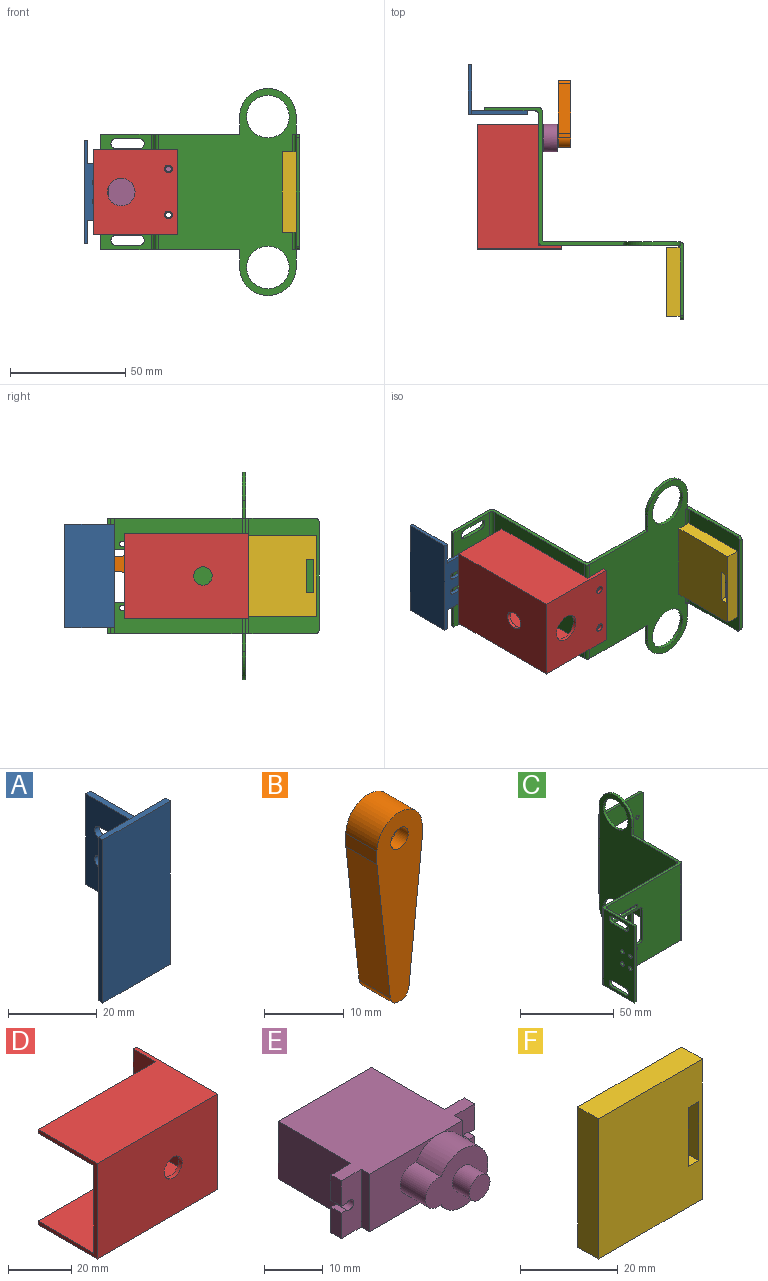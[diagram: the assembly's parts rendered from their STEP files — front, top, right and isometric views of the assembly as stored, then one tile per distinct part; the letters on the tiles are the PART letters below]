
ASSEMBLY  parts=6 mates=5
PART A: 18 faces, bbox 21.5x25.5x45 mm
  f0: plane 24x1.5mm, normal (0,0,1), area 36mm2, adj f3,f5,f6,f7
  f1: plane 24x1.5mm, normal (0,0,-1), area 36mm2, adj f3,f5,f6,f7
  f2: plane 45x21.5mm, normal (0,-1,0), area 967.5mm2, adj f4,f6,f16,f17
  f3: plane 45x21.5mm, normal (0,1,0), area 930mm2, adj f0,f1,f4,f6,f7,f16,f17
  f4: plane 45x1.5mm, normal (-1,0,0), area 67.5mm2, adj f2,f3,f16,f17
  f5: plane 25x1.5mm, normal (0,1,0), area 37.5mm2, adj f0,f1,f6,f7
  f6: plane 45x25.5mm, normal (1,0,0), area 549mm2, adj f0,f1,f2,f3,f5,f8,f9,f10
  f7: plane 25x24mm, normal (-1,0,0), area 481.5mm2, adj f0,f1,f3,f5,f8,f9,f10,f11
  f8: cylinder r=1.6mm len=3.2mm, axis (1,0,0), area 7.5mm2, adj f6,f7,f9,f11
  f9: plane 16x1.5mm, normal (0,0,-1), area 24mm2, adj f6,f7,f8,f10
  f10: cylinder r=1.6mm len=3.2mm, axis (1,0,0), area 7.5mm2, adj f6,f7,f9,f11
  f11: plane 16x1.5mm, normal (0,0,1), area 24mm2, adj f6,f7,f8,f10
  f12: cylinder r=1.6mm len=3.2mm, axis (1,0,0), area 7.5mm2, adj f6,f7,f13,f15
  f13: plane 16x1.5mm, normal (0,0,1), area 24mm2, adj f6,f7,f12,f14
  f14: cylinder r=1.6mm len=3.2mm, axis (1,0,0), area 7.5mm2, adj f6,f7,f13,f15
  f15: plane 16x1.5mm, normal (0,0,-1), area 24mm2, adj f6,f7,f12,f14
  f16: plane 21.5x1.5mm, normal (0,0,-1), area 32.3mm2, adj f2,f3,f4,f6
  f17: plane 21.5x1.5mm, normal (0,0,1), area 32.3mm2, adj f2,f3,f4,f6
PART B: 13 faces, bbox 8x5.5x29 mm
  f0: plane 5.5x0.31mm, normal (0,0,-1), area 1.7mm2, adj f3,f4,f11,f12
  f1: plane 5.5x2mm, normal (1,0,0), area 11mm2, adj f3,f4,f5,f10
  f2: plane 5.5x2mm, normal (-1,0,0), area 11mm2, adj f3,f4,f5,f9
  f3: plane 29x8mm, normal (0,1,0), area 148.8mm2, adj f0,f1,f2,f5,f6,f9,f10,f11
  f4: plane 29x8mm, normal (0,-1,0), area 159.3mm2, adj f0,f1,f2,f5,f8,f9,f10,f11
  f5: cylinder r=4mm len=8mm, axis (0,-1,0), area 69.1mm2, adj f1,f2,f3,f4
  f6: cylinder r=2.4mm len=4.8mm, axis (0,-1,0), area 52.8mm2, adj f3,f7
  f7: plane 4.8x4.8mm, normal (0,1,0), area 10.5mm2, adj f6,f8
  f8: cylinder r=1.55mm len=3.1mm, axis (0,1,0), area 19.5mm2, adj f4,f7
  f9: plane 21.66x5.5mm, normal (-0.99,0,-0.11), area 119.8mm2, adj f2,f3,f4,f11
  f10: plane 21.66x5.5mm, normal (0.99,0,-0.11), area 119.8mm2, adj f1,f3,f4,f12
  f11: cylinder r=1.5mm len=5.5mm, axis (0,1,0), area 12.1mm2, adj f0,f3,f4,f9
  f12: cylinder r=1.5mm len=5.5mm, axis (0,-1,0), area 12.1mm2, adj f0,f3,f4,f10
PART C: 72 faces, bbox 92x86.5x90 mm
  f0: plane 50x25mm, normal (1,0,0), area 1018.6mm2, adj f5,f6,f7,f37,f38,f39,f40,f41
  f1: plane 50x23.5mm, normal (-1,0,0), area 1033.6mm2, adj f5,f6,f7,f37,f38,f39,f40,f41
  f2: plane 50x30.5mm, normal (0,-1,0), area 1162.1mm2, adj f30,f31,f32,f33,f34,f35,f36,f51
  f3: plane 50x32mm, normal (0,1,0), area 1237.1mm2, adj f30,f31,f32,f33,f34,f35,f36,f51
  f4: plane 7.75x1.5mm, normal (0,1,0), area 11.6mm2, adj f21,f22,f28,f31
  f5: plane 60.5x60mm, normal (0,0,-1), area 178.5mm2, adj f0,f1,f7,f8,f20,f21,f22,f27
  f6: plane 60.5x60mm, normal (0,0,1), area 178.5mm2, adj f0,f1,f7,f8,f20,f21,f22,f26
  f7: plane 50x1.5mm, normal (0,-1,0), area 75mm2, adj f0,f1,f5,f6
  f8: plane 55.5x50mm, normal (0,1,0), area 2037.5mm2, adj f5,f6,f9,f10,f11,f12,f13,f14
  f9: cylinder r=1.2mm len=2.4mm, axis (0,1,0), area 5.7mm2, adj f8,f10,f19,f20
  f10: plane 18x1.5mm, normal (0,0,1), area 27mm2, adj f8,f9,f11,f20
  f11: cylinder r=1.2mm len=2.4mm, axis (0,1,0), area 5.7mm2, adj f8,f10,f19,f20
  f12: plane 25x1.5mm, normal (0,0,-1), area 37.5mm2, adj f8,f20,f68,f71
  f13: plane 20x1.5mm, normal (-1,0,0), area 30mm2, adj f8,f20,f68,f69
  f14: plane 25x1.5mm, normal (0,0,1), area 37.5mm2, adj f8,f20,f69,f70
  f15: plane 18x1.5mm, normal (0,0,-1), area 27mm2, adj f8,f16,f18,f20
  f16: cylinder r=1.2mm len=2.4mm, axis (0,1,0), area 5.7mm2, adj f8,f15,f17,f20
  f17: plane 18x1.5mm, normal (0,0,1), area 27mm2, adj f8,f16,f18,f20
  f18: cylinder r=1.2mm len=2.4mm, axis (0,1,0), area 5.7mm2, adj f8,f15,f17,f20
  f19: plane 18x1.5mm, normal (0,0,-1), area 27mm2, adj f8,f9,f11,f20
  f20: plane 55.5x50mm, normal (0,-1,0), area 2071mm2, adj f5,f6,f9,f10,f11,f12,f13,f14
  f21: plane 90x58.5mm, normal (-1,0,0), area 3228.8mm2, adj f4,f5,f6,f23,f24,f25,f26,f27
  f22: plane 90x60mm, normal (1,0,0), area 3228.8mm2, adj f4,f5,f6,f23,f24,f25,f26,f27
  f23: plane 7.75x1.5mm, normal (0,1,0), area 11.6mm2, adj f21,f22,f25,f30
  f24: cylinder r=9.25mm len=18.5mm, axis (1,0,0), area 87.2mm2, adj f21,f22
  f25: cylinder r=12.25mm len=24.5mm, axis (1,0,0), area 57.7mm2, adj f21,f22,f23,f26
  f26: plane 7.75x1.5mm, normal (0,-1,0), area 11.6mm2, adj f6,f21,f22,f25
  f27: plane 7.75x1.5mm, normal (0,-1,0), area 11.6mm2, adj f5,f21,f22,f28
  f28: cylinder r=12.25mm len=24.5mm, axis (1,0,0), area 57.7mm2, adj f4,f21,f22,f27
  f29: cylinder r=9.25mm len=18.5mm, axis (1,0,0), area 87.2mm2, adj f21,f22
  f30: plane 32x3mm, normal (0,0,1), area 48mm2, adj f2,f3,f22,f23,f55,f59,f67
  f31: plane 32x3mm, normal (0,0,-1), area 48mm2, adj f2,f3,f4,f22,f55,f59,f66
  f32: plane 47x1.5mm, normal (1,0,0), area 70.5mm2, adj f2,f3,f66,f67
  f33: plane 22.5x1.5mm, normal (1,0,0), area 33.8mm2, adj f2,f3,f62,f65
  f34: plane 10.5x1.5mm, normal (0,0,-1), area 15.8mm2, adj f2,f3,f62,f63
  f35: plane 22.5x1.5mm, normal (-1,0,0), area 33.8mm2, adj f2,f3,f63,f64
  f36: plane 10.5x1.5mm, normal (0,0,1), area 15.8mm2, adj f2,f3,f64,f65
  f37: plane 10x1.5mm, normal (0,0,-1), area 15mm2, adj f0,f1,f38,f40
  f38: cylinder r=2.25mm len=4.5mm, axis (1,0,0), area 10.6mm2, adj f0,f1,f37,f39
  f39: plane 10x1.5mm, normal (0,0,1), area 15mm2, adj f0,f1,f38,f40
  f40: cylinder r=2.25mm len=4.5mm, axis (1,0,0), area 10.6mm2, adj f0,f1,f37,f39
  f41: plane 10x1.5mm, normal (0,0,-1), area 15mm2, adj f0,f1,f42,f44
  f42: cylinder r=2.25mm len=4.5mm, axis (1,0,0), area 10.6mm2, adj f0,f1,f41,f43
  f43: plane 10x1.5mm, normal (0,0,1), area 15mm2, adj f0,f1,f42,f44
  f44: cylinder r=2.25mm len=4.5mm, axis (1,0,0), area 10.6mm2, adj f0,f1,f41,f43
  f45: cylinder r=1.25mm len=2.5mm, axis (1,0,0), area 11.8mm2, adj f0,f1
  f46: cylinder r=1.25mm len=2.5mm, axis (1,0,0), area 11.8mm2, adj f0,f1
  f47: cylinder r=1.25mm len=2.5mm, axis (1,0,0), area 11.8mm2, adj f0,f1
  f48: cylinder r=1.25mm len=2.5mm, axis (1,0,0), area 11.8mm2, adj f0,f1
  f49: cylinder r=1.25mm len=2.5mm, axis (1,0,0), area 11.8mm2, adj f21,f22
  f50: cylinder r=1.25mm len=2.5mm, axis (1,0,0), area 11.8mm2, adj f21,f22
  f51: cylinder r=1.25mm len=2.5mm, axis (0,-1,0), area 11.8mm2, adj f2,f3
  f52: cylinder r=1.25mm len=2.5mm, axis (0,-1,0), area 11.8mm2, adj f2,f3
  f53: cylinder r=1.25mm len=2.5mm, axis (0,-1,0), area 11.8mm2, adj f2,f3
  f54: cylinder r=1.25mm len=2.5mm, axis (0,-1,0), area 11.8mm2, adj f2,f3
  f55: cylinder r=1.5mm len=50mm, axis (0,0,-1), area 117.8mm2, adj f2,f22,f30,f31
  f56: cylinder r=1.5mm len=50mm, axis (0,0,-1), area 117.8mm2, adj f5,f6,f8,f21
  f57: cylinder r=1.5mm len=15mm, axis (0,0,1), area 33.1mm2, adj f0,f6,f20,f71
  f58: cylinder r=1.5mm len=15mm, axis (0,0,1), area 33.1mm2, adj f0,f5,f20,f70
  f59: cylinder r=1.5mm len=50mm, axis (0,0,-1), area 117.8mm2, adj f3,f21,f30,f31
  f60: cylinder r=1.5mm len=50mm, axis (0,0,1), area 117.8mm2, adj f5,f6,f20,f22
  f61: cylinder r=1.5mm len=50mm, axis (0,0,-1), area 117.8mm2, adj f0,f1,f5,f6,f8
  f62: cylinder r=1.5mm len=1.5mm, axis (0,1,0), area 3.5mm2, adj f2,f3,f33,f34
  f63: cylinder r=1.5mm len=1.5mm, axis (0,-1,0), area 3.5mm2, adj f2,f3,f34,f35
  f64: cylinder r=1.5mm len=1.5mm, axis (0,1,0), area 3.5mm2, adj f2,f3,f35,f36
  f65: cylinder r=1.5mm len=1.5mm, axis (0,-1,0), area 3.5mm2, adj f2,f3,f33,f36
  f66: cylinder r=1.5mm len=1.5mm, axis (0,-1,0), area 3.5mm2, adj f2,f3,f31,f32
  f67: cylinder r=1.5mm len=1.5mm, axis (0,1,0), area 3.5mm2, adj f2,f3,f30,f32
  f68: cylinder r=1.5mm len=1.5mm, axis (0,1,0), area 3.5mm2, adj f8,f12,f13,f20
  f69: cylinder r=1.5mm len=1.5mm, axis (0,-1,0), area 3.5mm2, adj f8,f13,f14,f20
  f70: cylinder r=1.5mm len=3mm, axis (0,-1,0), area 4.8mm2, adj f0,f8,f14,f58
  f71: cylinder r=1.5mm len=3mm, axis (0,1,0), area 4.8mm2, adj f0,f8,f12,f57
PART D: 16 faces, bbox 54x36.5x37 mm
  f0: plane 52.5x1.5mm, normal (0,1,0), area 78.7mm2, adj f4,f5,f6,f7
  f1: plane 52.5x1.5mm, normal (0,1,0), area 78.7mm2, adj f2,f3,f4,f6
  f2: plane 54x36.5mm, normal (0,0,1), area 1446mm2, adj f1,f4,f6,f8,f9,f12
  f3: plane 52.5x25mm, normal (0,0,-1), area 1312.5mm2, adj f1,f4,f6,f10
  f4: plane 37x35mm, normal (-1,0,0), area 1088.7mm2, adj f0,f1,f2,f3,f5,f7,f9,f10
  f5: plane 52.5x25mm, normal (0,0,1), area 1312.5mm2, adj f0,f4,f6,f10
  f6: plane 37x26.5mm, normal (-1,0,0), area 130.5mm2, adj f0,f1,f2,f3,f5,f7,f10,f12
  f7: plane 54x36.5mm, normal (0,0,-1), area 1446mm2, adj f0,f4,f6,f8,f9,f12
  f8: plane 37x36.5mm, normal (1,0,0), area 1219.2mm2, adj f2,f7,f9,f12,f13,f14,f15
  f9: plane 37x1.5mm, normal (0,1,0), area 55.5mm2, adj f2,f4,f7,f8
  f10: plane 52.5x34mm, normal (0,1,0), area 1734.7mm2, adj f3,f4,f5,f6,f11
  f11: cylinder r=4mm len=8mm, axis (0,1,0), area 37.7mm2, adj f10,f12
  f12: plane 54x37mm, normal (0,-1,0), area 1947.7mm2, adj f2,f6,f7,f8,f11
  f13: cylinder r=1.7mm len=3.4mm, axis (1,0,0), area 16mm2, adj f4,f8
  f14: cylinder r=1.7mm len=3.4mm, axis (1,0,0), area 16mm2, adj f4,f8
  f15: cylinder r=6mm len=12mm, axis (1,0,0), area 56.5mm2, adj f4,f8
PART E: 29 faces, bbox 32x32x12 mm
  f0: plane 17.5x12mm, normal (1,0,0), area 210mm2, adj f4,f6,f14,f27
  f1: plane 17.5x12mm, normal (-1,0,0), area 210mm2, adj f4,f6,f14,f20
  f2: plane 6x6mm, normal (0,-1,0), area 7.7mm2, adj f5,f6,f9
  f3: plane 6x6mm, normal (0,-1,0), area 7.7mm2, adj f4,f5,f9
  f4: plane 32x22mm, normal (0,0,-1), area 516.8mm2, adj f0,f1,f3,f5,f7,f8,f14,f19
  f5: plane 12x2mm, normal (1,0,0), area 24mm2, adj f2,f3,f4,f6,f28
  f6: plane 32x22mm, normal (0,0,1), area 516.8mm2, adj f0,f1,f2,f5,f7,f8,f14,f15
  f7: plane 12x2mm, normal (-1,0,0), area 24mm2, adj f4,f6,f8,f21
  f8: plane 16.4x12mm, normal (0,-1,0), area 124.6mm2, adj f4,f6,f7,f9,f10
  f9: cylinder r=6mm len=12mm, axis (0,1,0), area 189.8mm2, adj f2,f3,f8,f10,f11
  f10: cylinder r=3mm len=6mm, axis (0,1,0), area 65.6mm2, adj f8,f9,f11
  f11: plane 15x12mm, normal (0,-1,0), area 109.1mm2, adj f9,f10,f12
  f12: cylinder r=2.5mm len=5mm, axis (0,1,0), area 62.8mm2, adj f11,f13
  f13: plane 5x5mm, normal (0,-1,0), area 19.6mm2, adj f12
  f14: plane 22.4x12mm, normal (0,1,0), area 268.8mm2, adj f0,f1,f4,f6
  f15: plane 5.3x2.5mm, normal (-1,0,0), area 13.2mm2, adj f6,f16,f20,f21
  f16: plane 2.5x1.29mm, normal (0,0,-1), area 3.2mm2, adj f15,f17,f20,f21
  f17: cylinder r=1mm len=2.5mm, axis (0,-1,0), area 11.8mm2, adj f16,f18,f20,f21
  f18: plane 2.5x1.29mm, normal (0,0,1), area 3.2mm2, adj f17,f19,f20,f21
  f19: plane 5.3x2.5mm, normal (-1,0,0), area 13.2mm2, adj f4,f18,f20,f21
  f20: plane 12x4.8mm, normal (0,1,0), area 52.9mm2, adj f1,f4,f6,f15,f16,f17,f18,f19
  f21: plane 12x4.8mm, normal (0,-1,0), area 52.9mm2, adj f4,f6,f7,f15,f16,f17,f18,f19
  f22: plane 2.5x1.29mm, normal (0,0,1), area 3.2mm2, adj f23,f26,f27,f28
  f23: cylinder r=1mm len=2.5mm, axis (0,-1,0), area 11.8mm2, adj f22,f24,f27,f28
  f24: plane 2.5x1.29mm, normal (0,0,-1), area 3.2mm2, adj f23,f25,f27,f28
  f25: plane 5.3x2.5mm, normal (1,0,0), area 13.2mm2, adj f6,f24,f27,f28
  f26: plane 5.3x2.5mm, normal (1,0,0), area 13.2mm2, adj f4,f22,f27,f28
  f27: plane 12x4.8mm, normal (0,1,0), area 52.9mm2, adj f0,f4,f6,f22,f23,f24,f25,f26
  f28: plane 12x4.8mm, normal (0,-1,0), area 52.9mm2, adj f4,f5,f6,f22,f23,f24,f25,f26
PART F: 32 faces, bbox 30x6x35 mm
  f0: plane 27.9x3.5mm, normal (0,0,-1), area 83.7mm2, adj f1,f6,f11,f13,f18,f23,f25,f27
  f1: plane 6.6x1.3mm, normal (-1,0,0), area 8.6mm2, adj f0,f17,f23,f27
  f2: plane 6.6x1.3mm, normal (-1,0,0), area 8.6mm2, adj f3,f19,f24,f27
  f3: plane 27.9x3.5mm, normal (0,0,1), area 83.7mm2, adj f2,f4,f6,f13,f18,f22,f24,f27
  f4: plane 6.6x1.3mm, normal (1,0,0), area 8.6mm2, adj f3,f5,f22,f27
  f5: plane 5.35x1.3mm, normal (0,0,1), area 7mm2, adj f4,f6,f22,f27
  f6: plane 27.9x3.5mm, normal (1,0,0), area 80.5mm2, adj f0,f3,f5,f7,f13,f22,f25,f27
  f7: plane 5.35x1.3mm, normal (0,0,-1), area 7mm2, adj f6,f11,f25,f27
  f8: cylinder r=1.25mm len=2.5mm, axis (0,1,0), area 10.2mm2, adj f25,f31
  f9: cylinder r=1.25mm len=2.5mm, axis (0,1,0), area 10.2mm2, adj f24,f30
  f10: cylinder r=1.25mm len=2.5mm, axis (0,1,0), area 10.2mm2, adj f23,f29
  f11: plane 6.6x1.3mm, normal (1,0,0), area 8.6mm2, adj f0,f7,f25,f27
  f12: cylinder r=1.25mm len=2.5mm, axis (0,1,0), area 10.2mm2, adj f22,f26
  f13: plane 35x30mm, normal (0,1,0), area 271.6mm2, adj f0,f3,f6,f14,f15,f16,f18,f20
  f14: plane 30x6mm, normal (0,0,1), area 180mm2, adj f13,f15,f20,f21
  f15: plane 35x6mm, normal (-1,0,0), area 210mm2, adj f13,f14,f16,f21
  f16: plane 30x6mm, normal (0,0,-1), area 180mm2, adj f13,f15,f20,f21
  f17: plane 5.35x3.8mm, normal (0,0,-1), area 14.5mm2, adj f1,f18,f21,f23,f27,f28
  f18: plane 27.9x6mm, normal (-1,0,0), area 117.2mm2, adj f0,f3,f13,f17,f19,f21,f23,f24
  f19: plane 5.35x3.8mm, normal (0,0,1), area 14.5mm2, adj f2,f18,f21,f24,f27,f28
  f20: plane 35x6mm, normal (1,0,0), area 210mm2, adj f13,f14,f16,f21
  f21: plane 35x30mm, normal (0,-1,0), area 1005.9mm2, adj f14,f15,f16,f17,f18,f19,f20,f28
  f22: plane 6.6x5.35mm, normal (0,1,0), area 30.4mm2, adj f3,f4,f5,f6,f12
  f23: plane 6.6x5.35mm, normal (0,1,0), area 30.4mm2, adj f0,f1,f10,f17,f18
  f24: plane 6.6x5.35mm, normal (0,1,0), area 30.4mm2, adj f2,f3,f9,f18,f19
  f25: plane 6.6x5.35mm, normal (0,1,0), area 30.4mm2, adj f0,f6,f7,f8,f11
  f26: plane 2.5x2.5mm, normal (0,1,0), area 4.9mm2, adj f12
  f27: plane 27.9x24.9mm, normal (0,1,0), area 593.1mm2, adj f0,f1,f2,f3,f4,f5,f6,f7
  f28: plane 14.7x2.5mm, normal (1,0,0), area 36.8mm2, adj f17,f19,f21,f27
  f29: plane 2.5x2.5mm, normal (0,1,0), area 4.9mm2, adj f10
  f30: plane 2.5x2.5mm, normal (0,1,0), area 4.9mm2, adj f9
  f31: plane 2.5x2.5mm, normal (0,1,0), area 4.9mm2, adj f8
PLACE A rot(axis=(0,0,-1),90deg) t=(-55.4,-48.4,-90.38)mm
PLACE B rot(axis=(0.58,-0.58,0.58),120deg) t=(-51.9,-31.68,-90.38)mm
PLACE C rot(axis=(0,0,-1),90deg) t=(-50.4,-48.4,-90.38)mm fixed
PLACE D rot(axis=(0,0,-1),90deg) t=(-50.4,-48.4,-90.38)mm
PLACE E rot(axis=(0.58,-0.58,0.58),120deg) t=(-51.9,-31.68,-90.38)mm
PLACE F rot(axis=(0,0,-1),90deg) t=(-50.4,-48.4,-90.38)mm
MATE fastened F.f12 <-> C.f53  axis (1,0,0) through (7.4,-82.55,-100.73)mm
MATE fastened C.f50 <-> D.f14  axis (0,-1,0) through (-45.9,-78.4,-80.38)mm
MATE fastened C.f46 <-> A.f7  axis (0,-1,0) through (-66.4,-19.9,-86.38)mm
MATE revolute B.f8 <-> E.f12  axis (-1,0,0) through (-39.9,-31.68,-85.18)mm
MATE planar E.f23 <-> C.f11  axis (1,0,0) through (-51.9,-31.68,-76.38)mm
